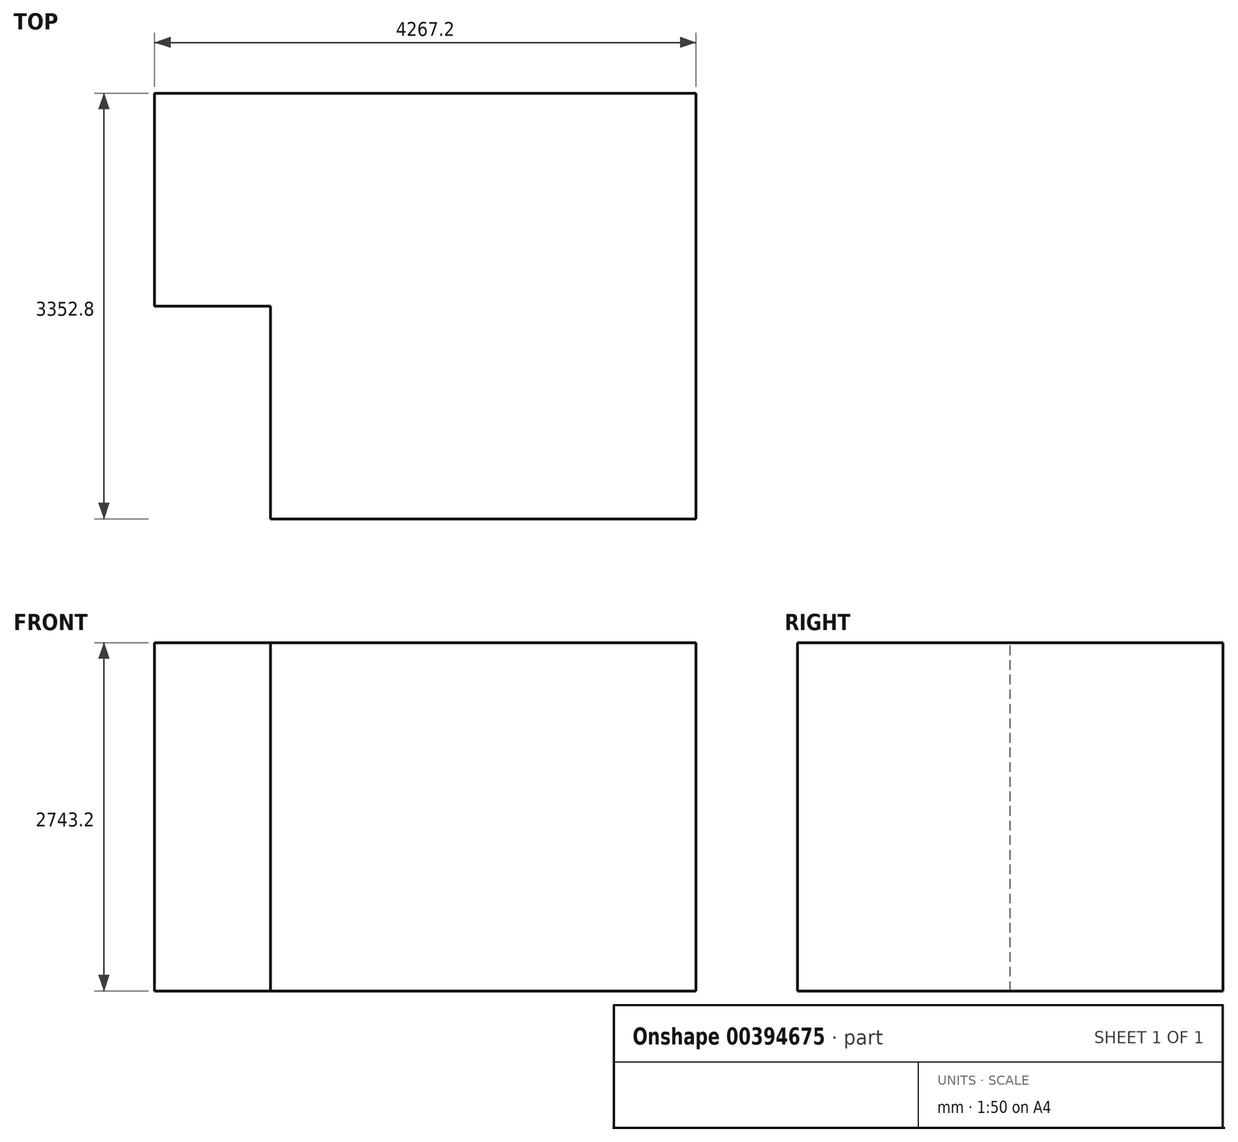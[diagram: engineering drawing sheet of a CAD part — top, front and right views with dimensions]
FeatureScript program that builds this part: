
annotation { "Feature Type Name" : "Feature", "Feature Type Description" : "" }
export const myFeature = defineFeature(function(context is Context, id is Id, definition is map)
    precondition{}
    {
        {
            var Q0;
            Q0=qCreatedBy(makeId("Top.planeOp"),FACE);
            var sketch = newSketch(context, id + "F0", { "sketchPlane" : qUnion([Q0])});
            skLineSegment(sketch, "E0", {"start": v(0, 0) * mm, "end": v(-1684.67, 0) * mm});
            skLineSegment(sketch, "E1", {"start": v(0, 0) * mm, "end": v(1668.13, 0) * mm});
            skLineSegment(sketch, "E2", {"start": v(1668.13, 0) * mm, "end": v(1668.13, 3352.8) * mm});
            skLineSegment(sketch, "E3", {"start": v(1668.13, 3352.8) * mm, "end": v(-2599.07, 3352.8) * mm});
            skLineSegment(sketch, "E4", {"start": v(-2599.07, 3352.8) * mm, "end": v(-2599.07, 1676.4) * mm});
            skLineSegment(sketch, "E5", {"start": v(-1684.67, 1676.4) * mm, "end": v(-2599.07, 1676.4) * mm});
            skLineSegment(sketch, "E6", {"start": v(-1684.67, 1676.4) * mm, "end": v(-1684.67, 0) * mm});
            skSolve(sketch);
        }
        {
            var Q0;
            Q0=sQuery(id+"F0.wireOp",EDGE,"E3");
            var Q1;
            Q1=sQuery(id+"F0.wireOp",EDGE,"E2");
            var Q2;
            Q2=sQuery(id+"F0.wireOp",EDGE,"E4");
            var Q3;
            Q3=sQuery(id+"F0.wireOp",EDGE,"E5");
            var Q4;
            Q4=sQuery(id+"F0.wireOp",EDGE,"E6");
            var Q5;
            Q5=sQuery(id+"F0.wireOp",EDGE,"E0");
            var Q6;
            Q6=sQuery(id+"F0.wireOp",EDGE,"E1");
            extrude(context, id + "F1", {"bodyType" : ToolBodyType.SURFACE, "surfaceEntities" : qUnion([Q0, Q1, Q2, Q3, Q4, Q5, Q6]), "depth" : 2743.2 * mm, "offsetDistance" : 25.4 * mm});
        }
    });
